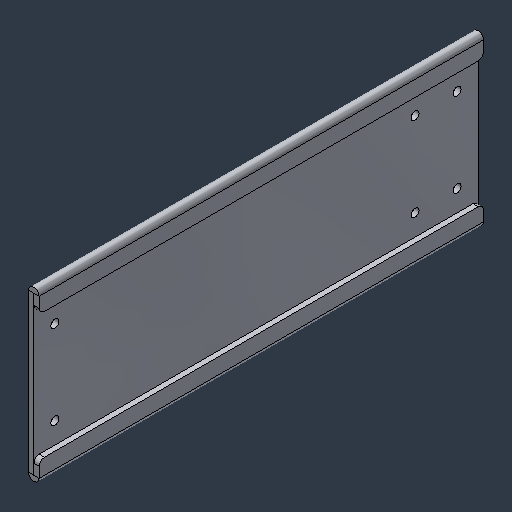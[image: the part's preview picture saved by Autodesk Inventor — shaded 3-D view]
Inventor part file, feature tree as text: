
AUTODESK INVENTOR PART (.ipt)
format: ipt  version: 2024.3 (Build 283343000, 343)  size: 118,272 bytes
history: native  units: mm (DEFAULTED — no unit token found)
features: fillet x1
ambient origin geometry x8: Origin, YZ Plane, XZ Plane, XY Plane, X Axis, Y Axis, Z Axis, Center Point
bodies: Solid1 (feature_tree)
feature tree (1):
  fillet  "Fillet1"  [1 undecoded]
note: 1 required parameter value undecoded (feature->parameter linkage not recoverable at this tier; creation-order binding heuristic only, values carry confidence <= 0.55)
